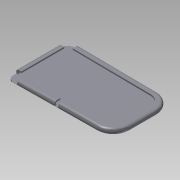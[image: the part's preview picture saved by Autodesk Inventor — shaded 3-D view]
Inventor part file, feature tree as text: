
AUTODESK INVENTOR PART (.ipt)
format: ipt  version: 2011 SP1 (Build 150282100, 282)  size: 259,584 bytes
history: native  units: mm
features: sketch x10, other x7, extrude x7, fillet x5, reference x2, sweep x1
ambient origin geometry x8: Origin, YZ Plane, XZ Plane, XY Plane, X Axis, Y Axis, Z Axis, Center Point
feature tree (32):
  other  "Твердое тело1"
  extrude  "Выдавливание1"  Depth=48.0mm
  extrude  "Выдавливание2"  Depth=25.0mm
  extrude  "Выдавливание3"  Depth=7.0mm
  sketch  "Эскиз4"
  other  "РабПлоскость1"
  sweep  "Сдвиг1"
  sketch  "Эскиз11"
  fillet  "Сопряжение3"  Radius=2.5mm
  fillet  "Сопряжение4"  Radius=2.5mm
  fillet  "Сопряжение5"  Radius=1.7mm
  extrude  "Выдавливание8"  Depth=1.1mm TaperAngle=0.0deg
  other  "РабПлоскость3"
  extrude  "Выдавливание9"  Depth=2.3mm
  fillet  "Сопряжение6"  [1 undecoded]
  fillet  "Сопряжение7"  Radius=40.0mm
  extrude  "Выдавливание10"  Depth=40.0mm
  extrude  "Выдавливание11"  Depth=2.5mm
  sketch  "Эскиз1"
  sketch  "Эскиз2"
  sketch  "Эскиз3"
  sketch  "Эскиз5"
  other  "Картинка1"
  sketch  "Эскиз12"
  reference  "Ссылка1"
  other  "РабПлоскость2"
  sketch  "Эскиз13"
  reference  "Ссылка2"
  sketch  "Эскиз14"
  sketch  "Эскиз15"
  other  "Проецирование ребер1"
  other  "Проецирование ребер2"
note: 1 required parameter value undecoded (feature->parameter linkage not recoverable at this tier; creation-order binding heuristic only, values carry confidence <= 0.55)
